FCSTD DOCUMENT  (FreeCAD 1.0R39109 (Git))
Label: Outline
License: All rights reserved
LicenseURL: http://en.wikipedia.org/wiki/All_rights_reserved
objects: Sketcher::SketchObject×1, PartDesign::Body×1
note: 3 computed .brp shape members not serialized (recipe doc carries the construction recipe); baked Part::Feature solids carry a one-line shape summary decoded from their .brp

FEATURE [Sketcher::SketchObject] Sketch
  ArcFitTolerance = 1e-06
  AttachmentSupport = -> [XY_Plane]
  FullyConstrained = true
  MakeInternals = false
  MapMode = 5
  sketch-geometry (14):
    g0: LineSegment StartX=-8.97 StartY=-3 StartZ=0 EndX=-8.97 EndY=-9.75 EndZ=0
    g1: LineSegment StartX=-8.22 StartY=-10.5 StartZ=0 EndX=15.82 EndY=-10.5 EndZ=0
    g2: LineSegment StartX=16.57 StartY=-9.75 StartZ=0 EndX=16.57 EndY=8.25 EndZ=0
    g3: LineSegment StartX=15.82 StartY=9 StartZ=0 EndX=5.25 EndY=9 EndZ=0
    g4: LineSegment StartX=5.25 StartY=9 StartZ=0 EndX=5.25 EndY=-3 EndZ=0
    g5: LineSegment StartX=5.25 StartY=-3 StartZ=0 EndX=-8.97 EndY=-3 EndZ=0
    g6: ArcOfCircle CenterX=-8.22 CenterY=-9.75 CenterZ=0 NormalX=0 NormalY=0 NormalZ=1 AngleXU=0 Radius=0.75 StartAngle=3.14159 EndAngle=4.71239
    g7: GeomPoint [constr] X=-8.97 Y=-10.5 Z=0
    g8: ArcOfCircle CenterX=15.82 CenterY=-9.75 CenterZ=0 NormalX=0 NormalY=0 NormalZ=1 AngleXU=0 Radius=0.75 StartAngle=4.71239 EndAngle=6.28319
    g9: GeomPoint [constr] X=16.57 Y=-10.5 Z=0
    g10: ArcOfCircle CenterX=15.82 CenterY=8.25 CenterZ=0 NormalX=0 NormalY=0 NormalZ=1 AngleXU=0 Radius=0.75 StartAngle=-9e-16 EndAngle=1.5708
    g11: GeomPoint [constr] X=16.57 Y=9 Z=0
    g12: GeomPoint X=-5.25 Y=-3 Z=0
    g13: GeomPoint X=8.97 Y=-3 Z=0
  constraints (32):
    c: Vertical(g0)
    c: Horizontal(g1)
    c: Vertical(g2)
    c: Coincident(g3,g4)
    c: Vertical(g4)
    c: Coincident(g4,g5)
    c: Coincident(g5,g0)
    c: DistanceY(g9,g11) = 19.5
    c: Horizontal(g3)
    c: Horizontal(g5)
    c: PointOnObject(g7,g0)
    c: PointOnObject(g7,g1)
    c: Tangent(g0,g6) = -1.5708
    c: Tangent(g1,g6) = -1.5708
    c: PointOnObject(g9,g2)
    c: PointOnObject(g9,g1)
    c: Tangent(g2,g8) = -1.5708
    c: Tangent(g1,g8) = -1.5708
    c: PointOnObject(g11,g3)
    c: PointOnObject(g11,g2)
    c: Tangent(g3,g10) = -1.5708
    c: Tangent(g2,g10) = -1.5708
    c: Equal(g10,g8)
    c: Equal(g8,g6)
    c: Radius(g6) = 0.75
    c: Symmetric(g4,g12,g-2)
    c: DistanceX(g12,g4) = 10.5
    c: DistanceY(g7,g0) = 7.5
    c: DistanceX(g0,g4) = 14.22
    c: DistanceY(g6,g-1) = 9.75
    c: Symmetric(g13,g0,g-2)
    c: DistanceX(g13,g11) = 7.6
FEATURE [PartDesign::Body] Body
  AllowCompound = false
  Group = -> [Sketch]
  Origin = -> Origin
